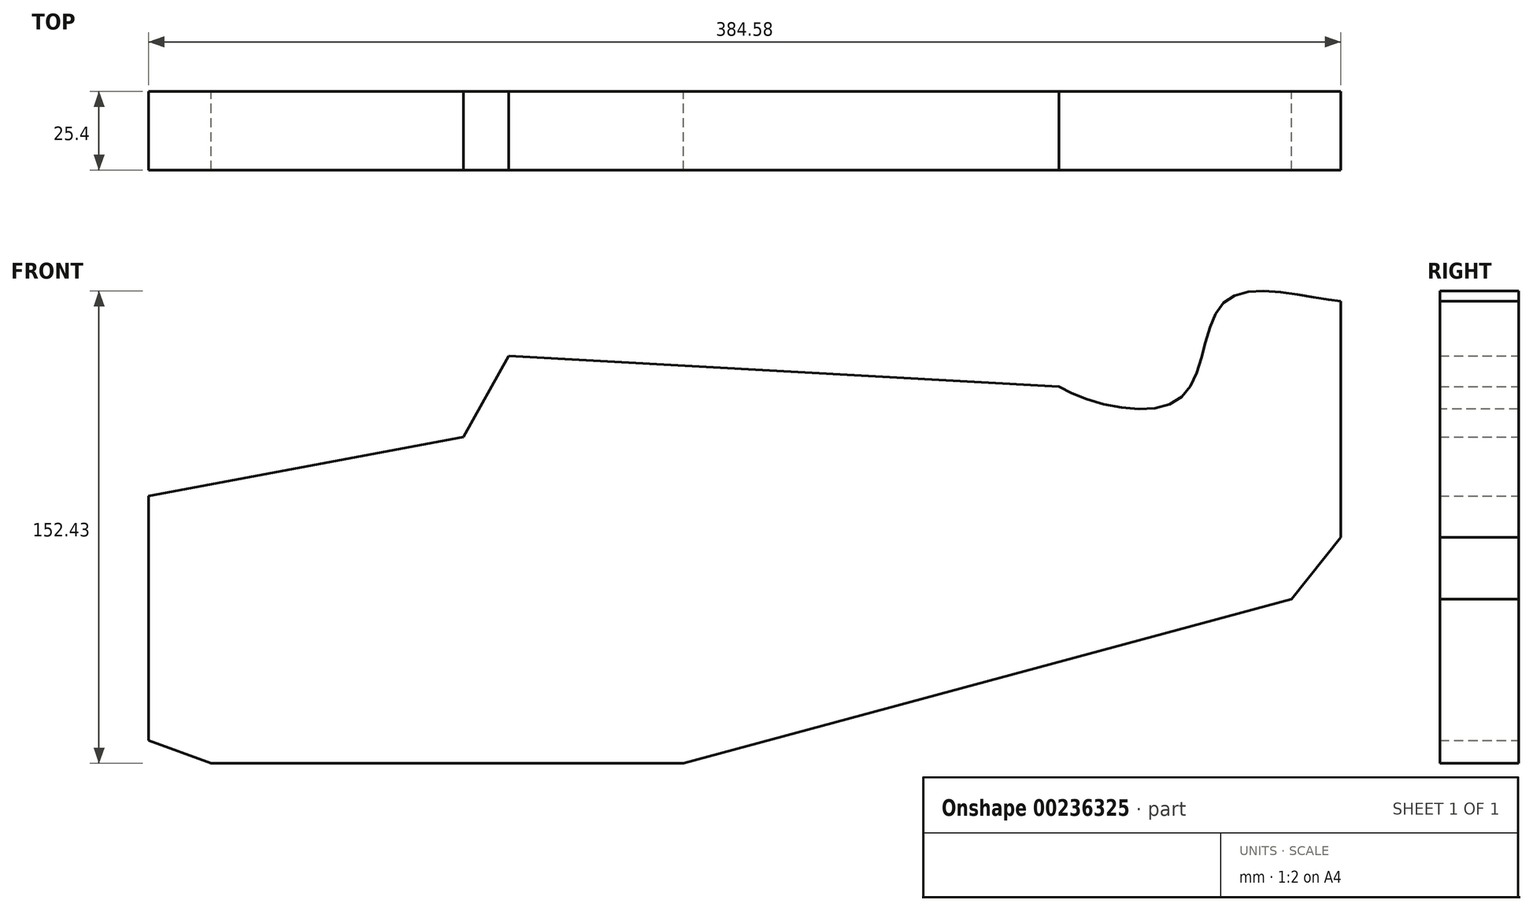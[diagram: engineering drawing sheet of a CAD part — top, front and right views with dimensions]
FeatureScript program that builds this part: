
annotation { "Feature Type Name" : "Feature", "Feature Type Description" : "" }
export const myFeature = defineFeature(function(context is Context, id is Id, definition is map)
    precondition{}
    {
        {
            var Q0;
            Q0=qCreatedBy(makeId("Front.planeOp"),FACE);
            var sketch = newSketch(context, id + "F0", { "sketchPlane" : qUnion([Q0])});
            skPoint(sketch, "E0.middle", {"position": v(0, 0) * mm});
            skLineSegment(sketch, "E1", {"start": v(-114.3, 28.58) * mm, "end": v(-215.9, 9.53) * mm});
            skLineSegment(sketch, "E2", {"start": v(-99.73, 54.72) * mm, "end": v(-114.3, 28.58) * mm});
            skLineSegment(sketch, "E3", {"start": v(-99.73, 54.72) * mm, "end": v(77.79, 44.78) * mm});
            skFitSpline(sketch, "E4", {"points": [v(77.79, 44.78) * mm, v(117.09, 41.24) * mm, v(132.1, 72.87) * mm, v(168.68, 72.35) * mm], "startDerivative": vector(84.68, -49.3) * mm, "endDerivative": vector(78.83, -5.48) * mm});
            skLineSegment(sketch, "E5", {"start": v(168.68, 72.35) * mm, "end": v(168.68, -3.85) * mm});
            skLineSegment(sketch, "E6", {"start": v(168.68, -3.85) * mm, "end": v(152.87, -23.73) * mm});
            skLineSegment(sketch, "E7", {"start": v(152.87, -23.73) * mm, "end": v(-43.3, -76.73) * mm});
            skLineSegment(sketch, "E8", {"start": v(-43.3, -76.73) * mm, "end": v(-195.7, -76.73) * mm});
            skLineSegment(sketch, "E9", {"start": v(-195.7, -76.73) * mm, "end": v(-215.9, -69.38) * mm});
            skLineSegment(sketch, "E10", {"start": v(-215.9, 9.53) * mm, "end": v(-215.9, -69.38) * mm});
            skSolve(sketch);
        }
        {
            var Q0;
            Q0 = qSketchRegion(id + "F0", true);
            extrude(context, id + "F1", {"entities" : qUnion([Q0]), "depth" : 25.4 * mm});
        }
    });
